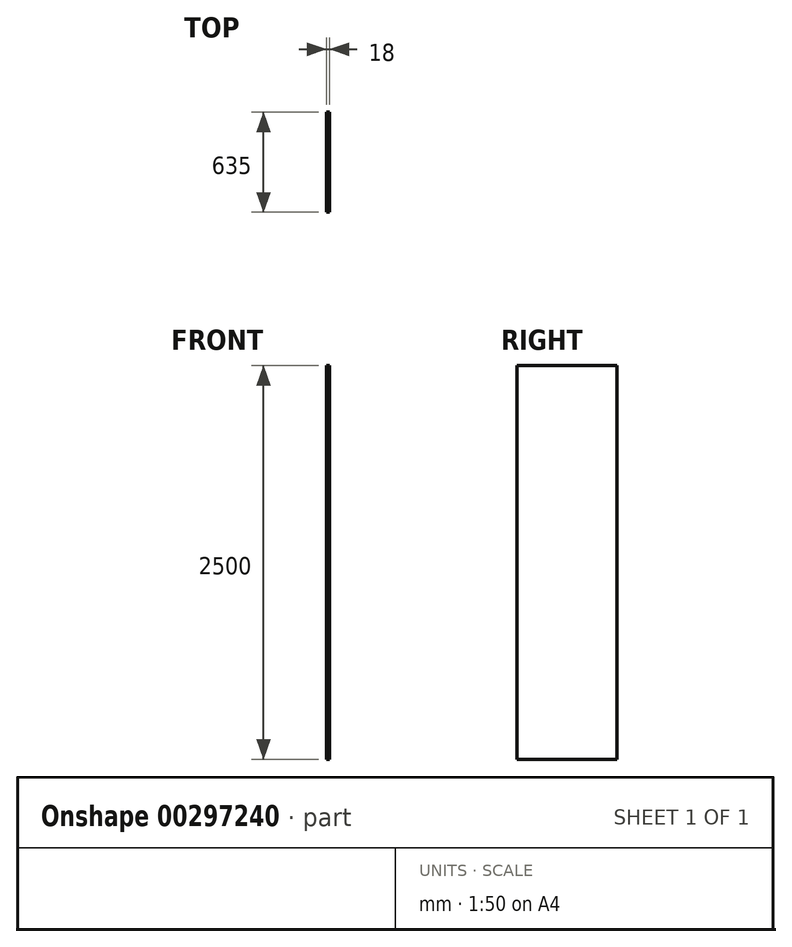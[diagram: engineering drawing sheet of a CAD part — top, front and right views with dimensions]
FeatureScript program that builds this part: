
annotation { "Feature Type Name" : "Feature", "Feature Type Description" : "" }
export const myFeature = defineFeature(function(context is Context, id is Id, definition is map)
    precondition{}
    {
        {
            var Q0;
            Q0=qCreatedBy(makeId("Right.planeOp"),FACE);
            var sketch = newSketch(context, id + "F0", { "sketchPlane" : qUnion([Q0])});
            skLineSegment(sketch, "E0.bottom", {"start": v(317.5, 1250) * mm, "end": v(-317.5, 1250) * mm});
            skLineSegment(sketch, "E0.top", {"start": v(317.5, -1250) * mm, "end": v(-317.5, -1250) * mm});
            skLineSegment(sketch, "E0.left", {"start": v(317.5, 1250) * mm, "end": v(317.5, -1250) * mm});
            skLineSegment(sketch, "E0.right", {"start": v(-317.5, 1250) * mm, "end": v(-317.5, -1250) * mm});
            skPoint(sketch, "E0.middle", {"position": v(0, 0) * mm});
            skSolve(sketch);
        }
        {
            var Q0;
            Q0=makeQuery(id+"F0.imprint","IMPRINT",FACE,{"disambiguationData":[TD([[makeQuery(id+"F0.imprint","IMPRINT",EDGE,{"derivedFrom":sQuery(id+"F0.wireOp",EDGE,"E0.bottom")}),1.0]])]});
            extrude(context, id + "F1", {"entities" : qUnion([Q0]), "depth" : 18 * mm});
        }
    });
